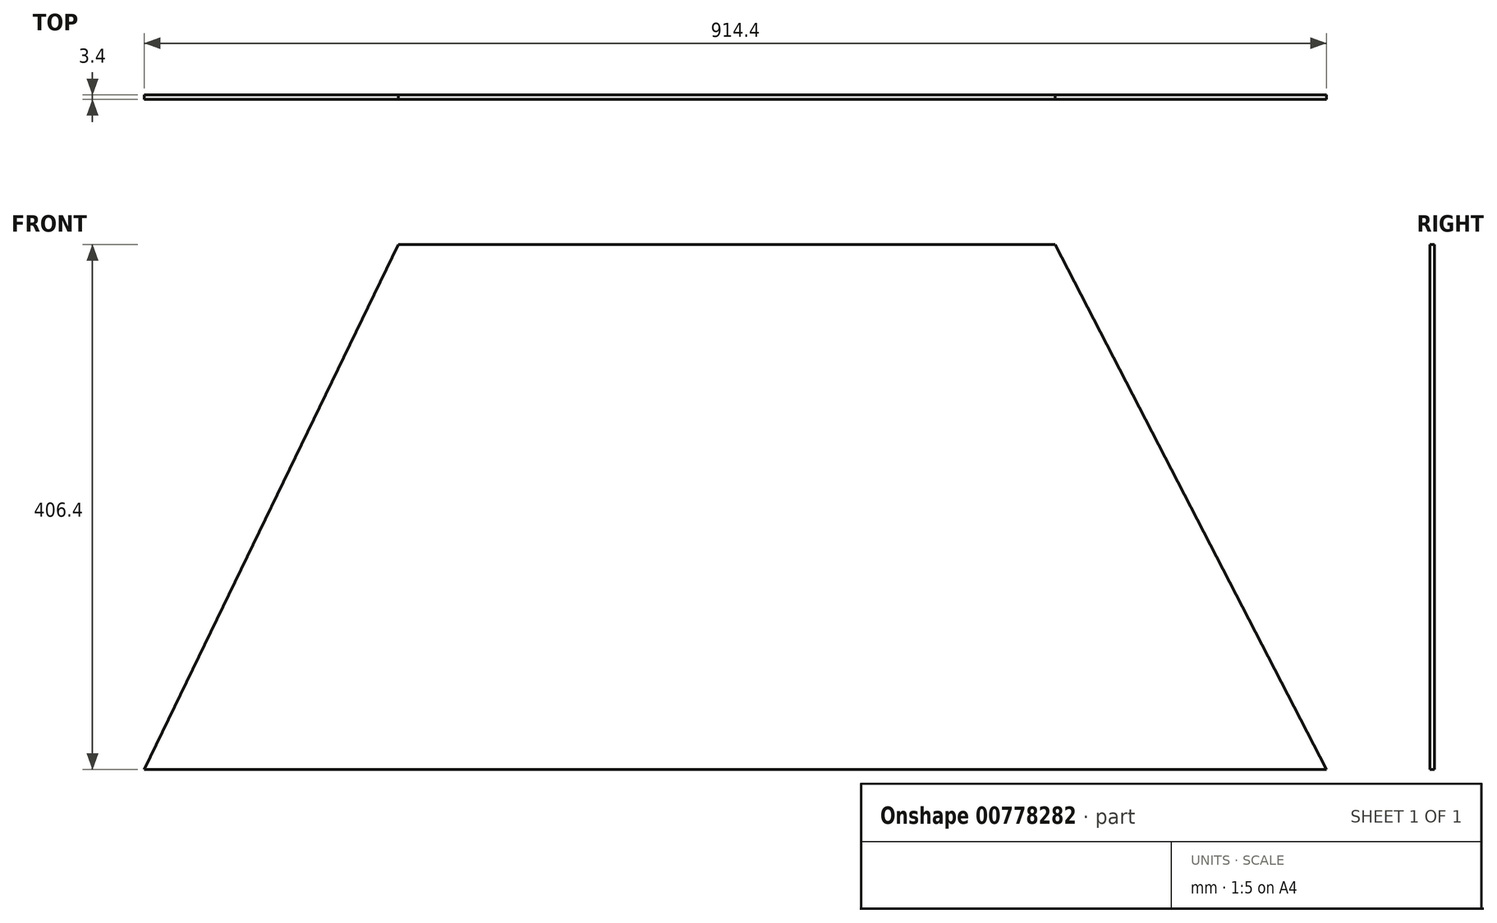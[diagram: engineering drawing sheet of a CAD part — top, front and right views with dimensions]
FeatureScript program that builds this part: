
annotation { "Feature Type Name" : "Feature", "Feature Type Description" : "" }
export const myFeature = defineFeature(function(context is Context, id is Id, definition is map)
    precondition{}
    {
        {
            var Q0;
            Q0=qCreatedBy(makeId("Front.planeOp"),FACE);
            var sketch = newSketch(context, id + "F0", { "sketchPlane" : qUnion([Q0])});
            skLineSegment(sketch, "E0", {"start": v(0, 0) * mm, "end": v(914.4, 0) * mm});
            skLineSegment(sketch, "E1", {"start": v(914.4, 0) * mm, "end": v(704.48, 406.4) * mm});
            skLineSegment(sketch, "E2", {"start": v(704.48, 406.4) * mm, "end": v(196.48, 406.4) * mm});
            skLineSegment(sketch, "E3", {"start": v(196.48, 406.4) * mm, "end": v(0, 0) * mm});
            skSolve(sketch);
        }
        {
            var Q0;
            Q0 = qSketchRegion(id + "F0", true);
            extrude(context, id + "F1", {"entities" : qUnion([Q0]), "depth" : 3.4 * mm, "offsetDistance" : 25.4 * mm});
        }
    });
